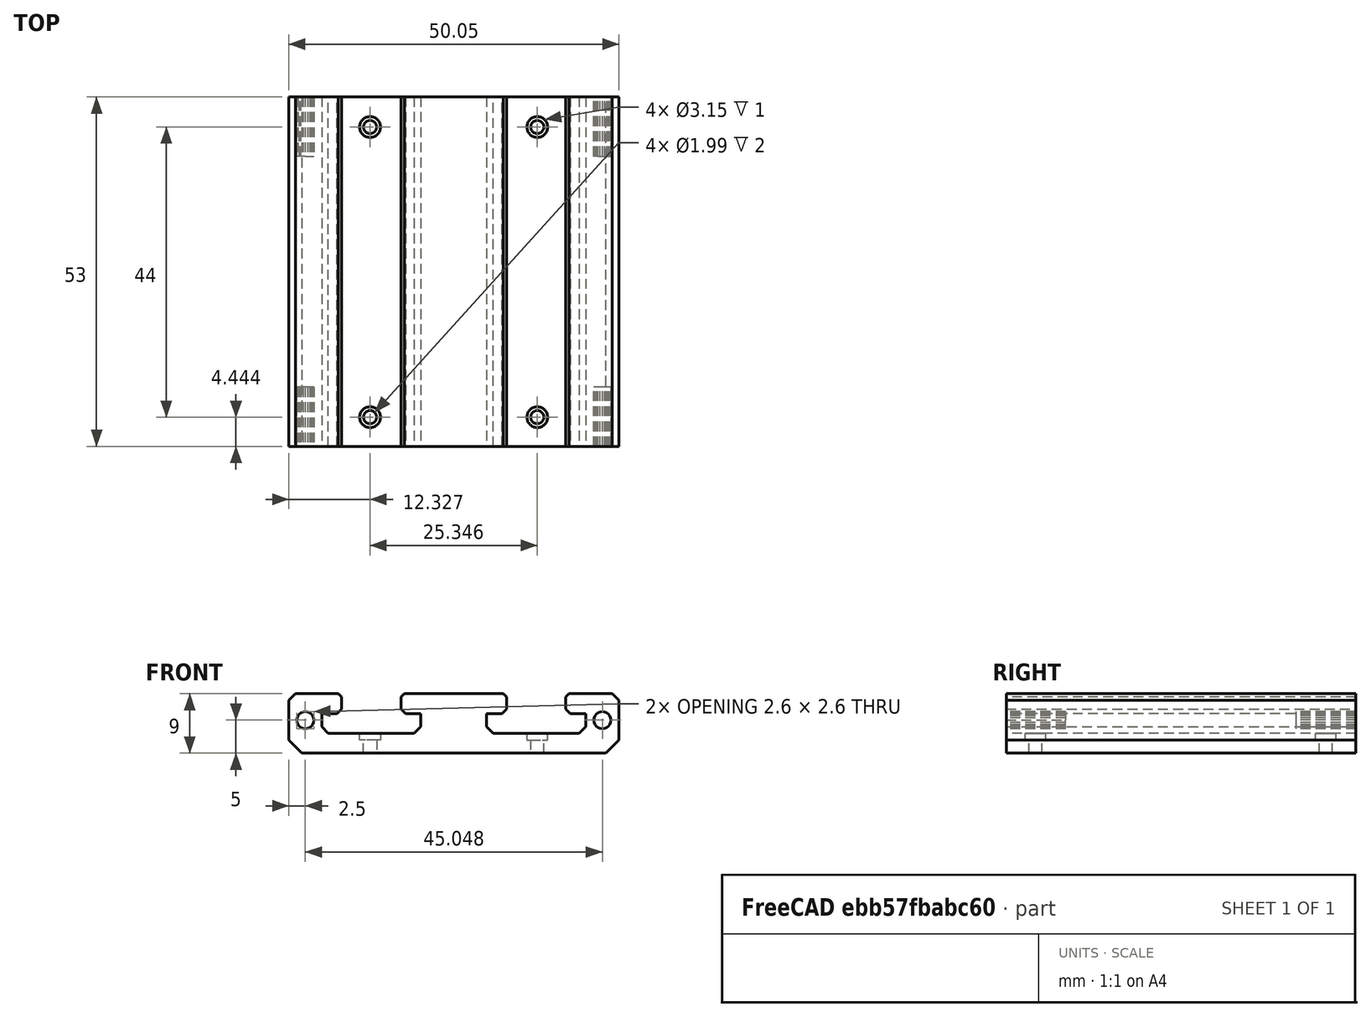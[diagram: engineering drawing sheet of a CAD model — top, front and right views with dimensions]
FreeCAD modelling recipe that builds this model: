
FCSTD DOCUMENT  (FreeCAD 0.19R24267 +148 (Git))
Label: Linear stage Base
License: All rights reserved
LicenseURL: http://en.wikipedia.org/wiki/All_rights_reserved
objects: PartDesign::Pocket×2, Part::Feature×1, PartDesign::FeatureBase×1, Sketcher::SketchObject×1, PartDesign::LinearPattern×1, PartDesign::Mirrored×1, PartDesign::MultiTransform×1, PartDesign::Body×1
note: 11 computed .brp shape members not serialized (recipe doc carries the construction recipe); baked Part::Feature solids carry a one-line shape summary decoded from their .brp

FEATURE [Part::Feature] Solid
  shape: bbox 50.05 x 53 x 9 mm, 138 faces (baked)
FEATURE [PartDesign::FeatureBase] BaseFeature
  BaseFeature = -> Solid
FEATURE [Sketcher::SketchObject] Sketch
  FullyConstrained = false
  MapMode = 5
  Placement = pos=(0,0,-25) rot=(0,0,1;0rad)
  Support = -> [BaseFeature]
  sketch-geometry (2):
    g0: Circle CenterX=-12.6729 CenterY=48.4435 CenterZ=0 NormalX=0 NormalY=0 NormalZ=1 AngleXU=0 Radius=0.995727
    g1: Circle CenterX=-12.6729 CenterY=48.4435 CenterZ=0 NormalX=0 NormalY=0 NormalZ=1 AngleXU=0 Radius=1.57438
  constraints (1):
    c: Coincident(g1,g0)
FEATURE [PartDesign::Pocket] Pocket
  BaseFeature = -> BaseFeature
  Length = 1
  Length2 = 100
  Profile = -> Sketch
  Type = 0
FEATURE [PartDesign::Pocket] Pocket001
  BaseFeature = -> Pocket
  Length = 5
  Length2 = 100
  Profile = -> Pocket [Edge402]
  Type = 0
FEATURE [PartDesign::LinearPattern] LinearPattern
  Direction = -> Y_Axis
  Length = 44
  Occurrences = 2
  Reversed = true
FEATURE [PartDesign::Mirrored] Mirrored
  MirrorPlane = -> Sketch [V_Axis]
FEATURE [PartDesign::MultiTransform] MultiTransform
  BaseFeature = -> Pocket001
  Originals = -> [Pocket,Pocket001]
  Transformations = -> [LinearPattern,Mirrored]
FEATURE [PartDesign::Body] Body
  BaseFeature = -> Solid
  Group = -> [BaseFeature,Sketch,Pocket,Pocket001,MultiTransform,LinearPattern,Mirrored]
  Origin = -> Origin
  Tip = -> MultiTransform
